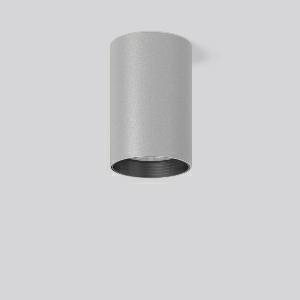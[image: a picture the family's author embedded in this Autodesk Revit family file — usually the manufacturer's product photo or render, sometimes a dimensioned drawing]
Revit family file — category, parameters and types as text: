
# Revit family: heledon_maxi_a_931248_004_2_76_b83c
name_source: partatom
category: Lighting Fixtures
units: mm (PartAtom-declared; Revit-internal decimal feet)

## family parameters
Cut with Voids When Loaded = No
Host = Face
Light Source = No
Part Type = Normal
Room Calculation Point = No
Round Connector Dimension = Use Diameter
Shared = No

## types (1)
- HELEDON maxi A (1 x LED Modul 927 bakery, 2950 lm, 2700)
    Apparent Load = 33 VA
    Approval mark = CE
    CIE Flux Codes = 97 100 100 100 100
    Color Rendering = 90
    Color Temperature = 2700
    Default Elevation = 1800 mm
    Description = Series: HELEDON maxi
Cylindrical surface-mounted downlight. Housing: die-cast aluminium, powder-coated. Internal ceiling frame polycarbonate with bayonet mounting. Black plastic ring and recessed LED to prevent glare from the side. Optical assembly with lens made of plastic (polycarbonate) for the best homogeneous light distribution - can be changed without tools. Special LED for illumination of pastries included. Suitable for Ceiling mounting. Easy installation with a separate ceiling frame with bayonet mounting and plug connection. Driver integrated. Connected via plug-in connector. High quality converter without flickering and stroboscopic effect. The following accessories can be mounted without use of tools: interchangeable lenses, decorative glasses, honeycomb louvre, clear and frosted diffusers, white interchangeable plastic ring. 
Colour: silver
Diameter: 123 mm
Height: 183 mm
Lamp: LED
Socket: without socket
Colour temperature: bakery
Colour rendering index (CRI): 97
System power: 33 W
Rated luminous flux: 2950 lm
Luminous efficiency: 89 lm/W
Control gear: Converter, dimmable, DALI
Protection class: I
Type of protection: IP 20
    Height = 183 mm
    Lamp = 1 x LED Modul 927 bakery
    Lamp Light Flux = 2950 lm
    Lamp count = 1
    Length = 123 mm
    Lifetime = 50000 h
    Luminous efficacy = 89 lm/W
    Manufacturer = RZB
    ModVariant = No
    Model = 931248.004.2.76
    Mounting Place = Ceiling
    Mounting Type = Surface mounted
    Number of Poles = 1
    OnlyDefault = Yes
    Power Factor = 1
    Product Name = HELEDON maxi A
    Product group = Surface mounted downlights
    ProductGroupID = 302
    Protection Class = Protection class I
    Protection Degree = IP 20
    RLX_Detail_Level = 1
    RLX_Emergency_Light_Flux = 0 lm
    RLX_Emergency_Type = 0
    RLX_Emergency_Type_DB = No
    RlxData = <blob elided: 99741 chars, md5=0f7ca188>
    Socket = socket
    Standby Power = 0 W
    System Light Flux = 2950 lm
    System Power = 33 W
    Type Comments = Product without accessories
    Type Image = 931193.004.jpg
    URL = http://relux.com
    VarID = ---
    Voltage = 230 V
    Voltage Range = 220-240 V
    Weight = 0.00 kg
    Width = 0 mm  [stored 0 ft]

note: [stored X ft] marks values corroborated as IEEE doubles in the binary element streams (Revit-internal decimal feet)

## geometry (parser evidence)
native form markers: Blend x4, Sweep x9
no freeform markers — native parametric forms only
